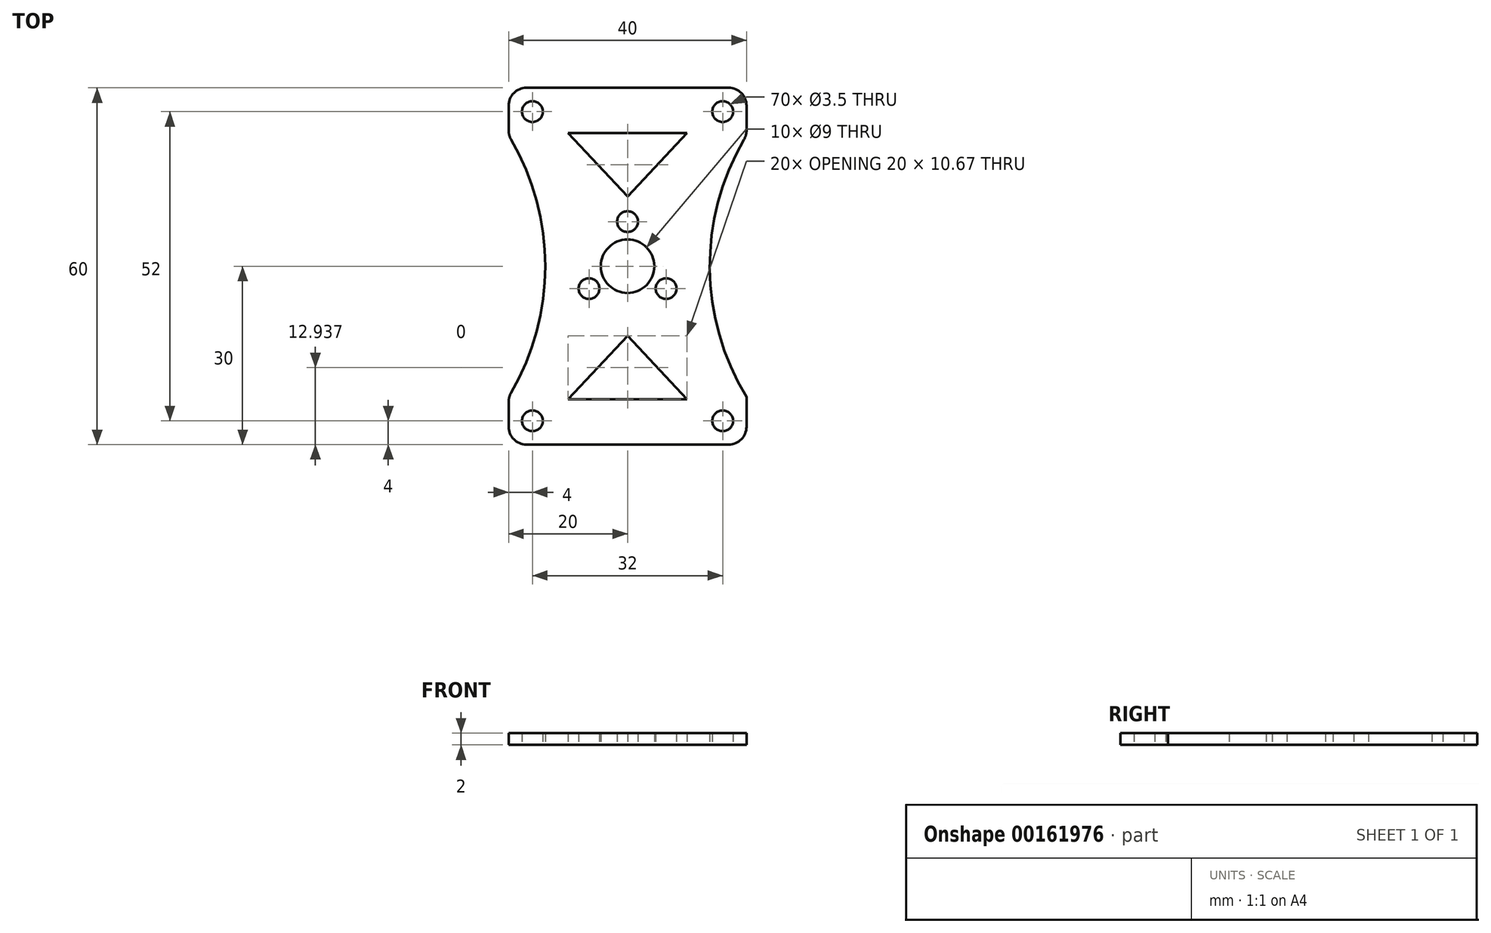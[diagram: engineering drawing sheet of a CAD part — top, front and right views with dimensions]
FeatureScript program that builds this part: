
annotation { "Feature Type Name" : "Feature", "Feature Type Description" : "" }
export const myFeature = defineFeature(function(context is Context, id is Id, definition is map)
    precondition{}
    {
        {
            var Q0;
            Q0=qCreatedBy(makeId("Top.planeOp"),FACE);
            var sketch = newSketch(context, id + "F0", { "sketchPlane" : qUnion([Q0])});
            skLineSegment(sketch, "E0.bottom", {"start": v(-20, 30) * mm, "end": v(20, 30) * mm});
            skLineSegment(sketch, "E0.top", {"start": v(-20, -30) * mm, "end": v(20, -30) * mm});
            skLineSegment(sketch, "E0.left", {"start": v(-20, 30) * mm, "end": v(-20, -30) * mm});
            skLineSegment(sketch, "E0.right", {"start": v(20, 30) * mm, "end": v(20, -30) * mm});
            skPoint(sketch, "E0.middle", {"position": v(0, 0) * mm});
            skCircle(sketch, "E1", {"center": v(-16, 26) * mm, "radius": 1.75 * mm});
            skCircle(sketch, "E2.MirrorC", {"center": v(16, 26) * mm, "radius": 1.75 * mm});
            skCircle(sketch, "E3.MirrorC", {"center": v(-16, -26) * mm, "radius": 1.75 * mm});
            skCircle(sketch, "E4.MirrorC", {"center": v(16, -26) * mm, "radius": 1.75 * mm});
            skLineSegment(sketch, "E5", {"start": v(0, -22.4) * mm, "end": v(10, -22.4) * mm});
            skLineSegment(sketch, "E6", {"start": v(10, -22.4) * mm, "end": v(0, -11.73) * mm});
            skLineSegment(sketch, "E7.MirrorCS", {"start": v(-10, -22.4) * mm, "end": v(0, -11.73) * mm});
            skLineSegment(sketch, "E8.MirrorCS", {"start": v(0, -22.4) * mm, "end": v(-10, -22.4) * mm});
            skLineSegment(sketch, "E9.MirrorCS", {"start": v(10, 22.4) * mm, "end": v(0, 11.73) * mm});
            skLineSegment(sketch, "E10.MirrorCS", {"start": v(-10, 22.4) * mm, "end": v(0, 11.73) * mm});
            skLineSegment(sketch, "E11.MirrorCS", {"start": v(0, 22.4) * mm, "end": v(10, 22.4) * mm});
            skLineSegment(sketch, "E12.MirrorCS", {"start": v(0, 22.4) * mm, "end": v(-10, 22.4) * mm});
            skArc(sketch, "E13", {"start": v(-20, -22) * mm, "mid": v(-13.83, 0) * mm, "end": v(-20, 22) * mm});
            skArc(sketch, "E14.MirrorCS", {"start": v(20, -22) * mm, "mid": v(13.83, 0) * mm, "end": v(20, 22) * mm});
            skCircle(sketch, "E15", {"center": v(0, 0) * mm, "radius": 4.5 * mm});
            skCircle(sketch, "E16", {"center": v(0, 0) * mm, "radius": 7.5 * mm, "construction": true});
            skCircle(sketch, "E17", {"center": v(0, 7.5) * mm, "radius": 1.75 * mm});
            skCircle(sketch, "E18", {"center": v(6.49, -3.77) * mm, "radius": 1.75 * mm});
            skCircle(sketch, "E19.MirrorC", {"center": v(-6.49, -3.77) * mm, "radius": 1.75 * mm});
            skSolve(sketch);
        }
        {
            var Q0;
            {var subQ27=sQuery(id+"F0.wireOp",EDGE,"E0.bottom");Q0=makeQuery(id+"F0.imprint","IMPRINT",FACE,{"disambiguationData":[TD([[makeQuery(id+"F0.imprint","IMPRINT",EDGE,{"derivedFrom":subQ27}),-1.0]])]});}
            extrude(context, id + "F1", {"entities" : qUnion([Q0]), "depth" : 2 * mm});
        }
        {
            var Q0;
            Q0=makeQuery(id+"F1.opExtrude","SWEPT_EDGE",EDGE,{"disambiguationData":[OSD([sQuery(id+"F0.wireOp",EDGE,"E0.bottom"),sQuery(id+"F0.wireOp",EDGE,"E0.left")])]});
            var Q1;
            Q1=makeQuery(id+"F1.opExtrude","SWEPT_EDGE",EDGE,{"disambiguationData":[OSD([sQuery(id+"F0.wireOp",EDGE,"E0.top"),sQuery(id+"F0.wireOp",EDGE,"E0.left")])]});
            var Q2;
            Q2=makeQuery(id+"F1.opExtrude","SWEPT_EDGE",EDGE,{"disambiguationData":[OSD([sQuery(id+"F0.wireOp",EDGE,"E0.top"),sQuery(id+"F0.wireOp",EDGE,"E0.right")])]});
            var Q3;
            Q3=makeQuery(id+"F1.opExtrude","SWEPT_EDGE",EDGE,{"disambiguationData":[OSD([sQuery(id+"F0.wireOp",EDGE,"E0.bottom"),sQuery(id+"F0.wireOp",EDGE,"E0.right")])]});
            var Q4;
            {var subQ0=sQuery(id+"F0.wireOp",EDGE,"E14.MirrorCS");var subQ1=sQuery(id+"F0.wireOp",EDGE,"E0.right");Q4=makeQuery(id+"F1.opExtrude","SWEPT_EDGE",EDGE,{"disambiguationData":[OSD([subQ1,subQ0]),TDD([makeQuery(id+"F0.imprint","INTERSECT",VERTEX,{"disambiguationData":[OD(0.0)],"derivedFrom":[subQ1,subQ0]})])]});}
            var Q5;
            {var subQ0=sQuery(id+"F0.wireOp",EDGE,"E13");var subQ1=sQuery(id+"F0.wireOp",EDGE,"E0.left");Q5=makeQuery(id+"F1.opExtrude","SWEPT_EDGE",EDGE,{"disambiguationData":[OSD([subQ1,subQ0]),TDD([makeQuery(id+"F0.imprint","INTERSECT",VERTEX,{"disambiguationData":[OD(0.0)],"derivedFrom":[subQ1,subQ0]})])]});}
            var Q6;
            {var subQ0=sQuery(id+"F0.wireOp",EDGE,"E13");var subQ1=sQuery(id+"F0.wireOp",EDGE,"E0.left");Q6=makeQuery(id+"F1.opExtrude","SWEPT_EDGE",EDGE,{"disambiguationData":[OSD([subQ1,subQ0]),TDD([makeQuery(id+"F0.imprint","INTERSECT",VERTEX,{"disambiguationData":[OD(1.0)],"derivedFrom":[subQ1,subQ0]})])]});}
            fillet(context, id + "F2", {"entities" : qUnion([Q0, Q1, Q2, Q3, Q4, Q5, Q6]), "radius" : 3 * mm, "tangentPropagation" : true, "allowEdgeOverflow" : false});
        }
    });
